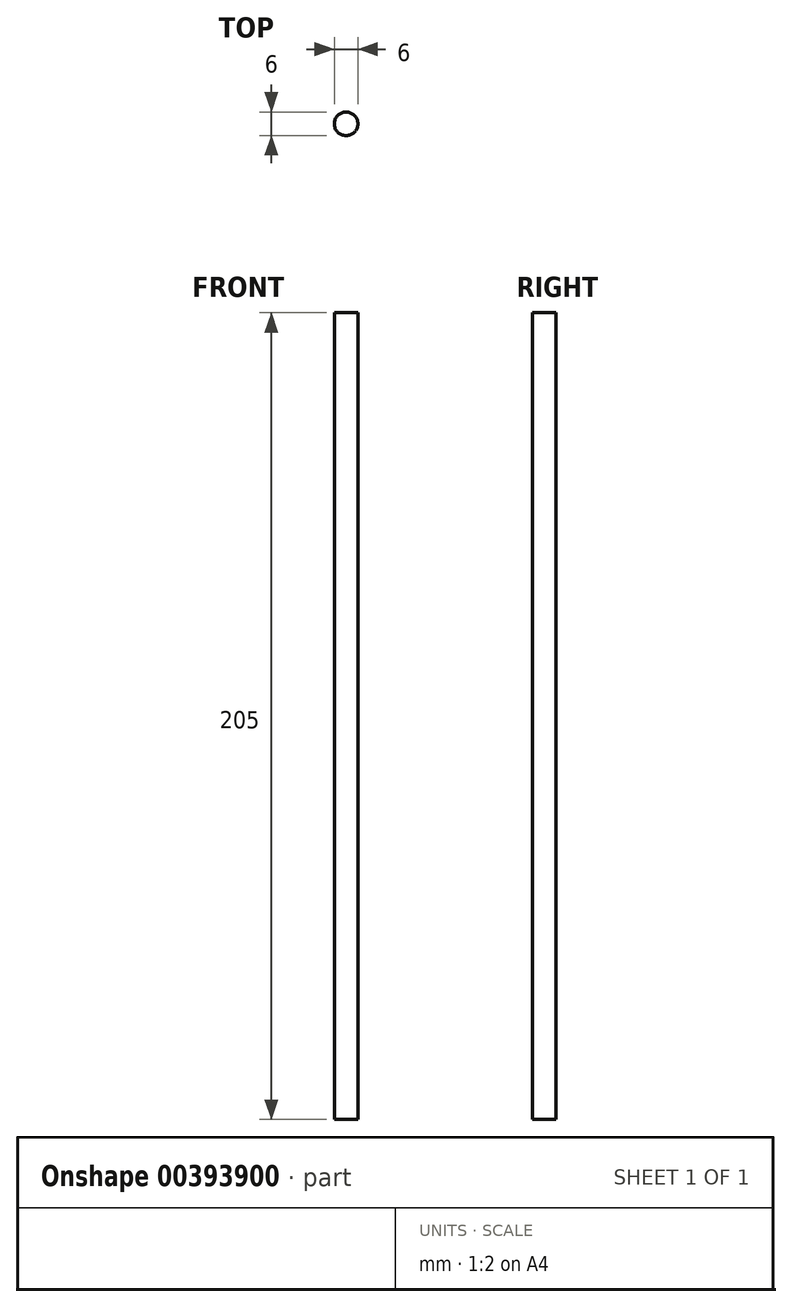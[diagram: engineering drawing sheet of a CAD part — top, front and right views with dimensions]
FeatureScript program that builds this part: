
annotation { "Feature Type Name" : "Feature", "Feature Type Description" : "" }
export const myFeature = defineFeature(function(context is Context, id is Id, definition is map)
    precondition{}
    {
        {
            var Q0;
            Q0=qCreatedBy(makeId("Top.planeOp"),FACE);
            var sketch = newSketch(context, id + "F0", { "sketchPlane" : qUnion([Q0])});
            skCircle(sketch, "E0", {"center": v(0, 0) * mm, "radius": 3 * mm});
            skSolve(sketch);
        }
        {
            var Q0;
            Q0=makeQuery(id+"F0.imprint","IMPRINT",FACE,{"disambiguationData":[TD([[makeQuery(id+"F0.imprint","IMPRINT",EDGE,{"derivedFrom":sQuery(id+"F0.wireOp",EDGE,"E0")}),1.0]])]});
            extrude(context, id + "F1", {"entities" : qUnion([Q0]), "depth" : 205 * mm, "offsetDistance" : 25 * mm});
        }
    });
